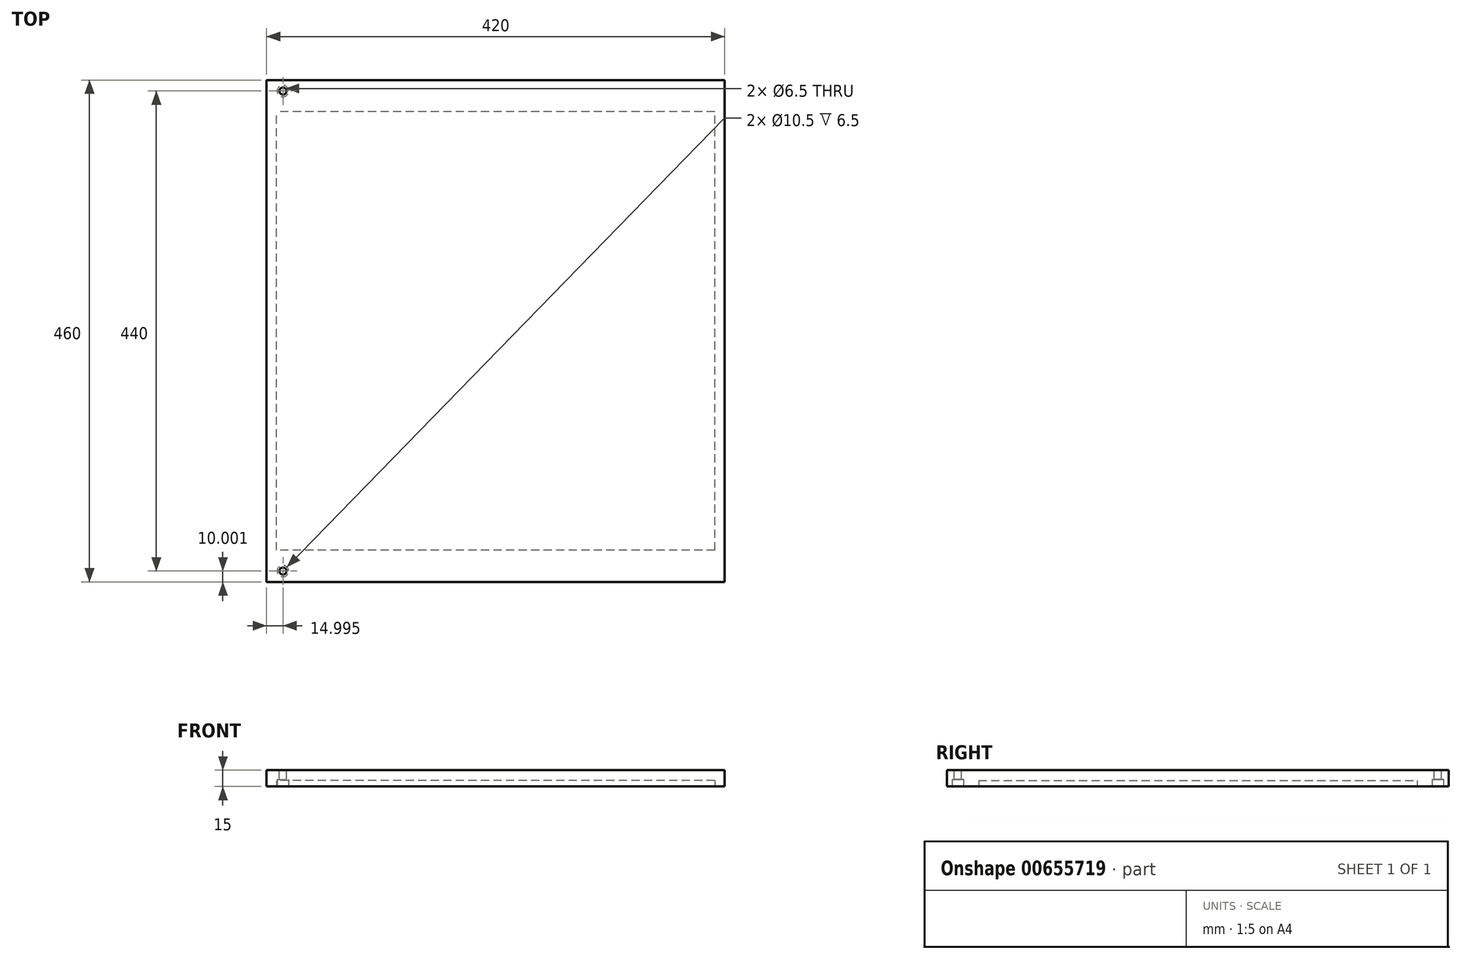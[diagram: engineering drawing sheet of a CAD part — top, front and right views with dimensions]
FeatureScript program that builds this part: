
annotation { "Feature Type Name" : "Feature", "Feature Type Description" : "" }
export const myFeature = defineFeature(function(context is Context, id is Id, definition is map)
    precondition{}
    {
        {
            var Q0;
            Q0=qCreatedBy(makeId("Top.planeOp"),FACE);
            var sketch = newSketch(context, id + "F0", { "sketchPlane" : qUnion([Q0])});
            skLineSegment(sketch, "E0.bottom", {"start": v(-74.43, -51.4) * mm, "end": v(345.57, -51.4) * mm});
            skLineSegment(sketch, "E0.top", {"start": v(-74.43, 408.6) * mm, "end": v(345.57, 408.6) * mm});
            skLineSegment(sketch, "E0.left", {"start": v(-74.43, -51.4) * mm, "end": v(-74.43, 408.6) * mm});
            skLineSegment(sketch, "E0.right", {"start": v(345.57, -51.4) * mm, "end": v(345.57, 408.6) * mm});
            skSolve(sketch);
        }
        {
            var Q0;
            Q0=makeQuery(id+"F0.imprint","IMPRINT",FACE,{"disambiguationData":[TD([[makeQuery(id+"F0.imprint","IMPRINT",EDGE,{"derivedFrom":sQuery(id+"F0.wireOp",EDGE,"E0.bottom")}),1.0]])]});
            extrude(context, id + "F1", {"entities" : qUnion([Q0]), "depth" : 15 * mm, "offsetDistance" : 25 * mm});
        }
        {
            var Q0;
            Q0=makeQuery(id+"F1.opExtrude","CAP_FACE",FACE,{"disambiguationData":[OSD([sQuery(id+"F0.wireOp",EDGE,"E0.bottom"),sQuery(id+"F0.wireOp",EDGE,"E0.top"),sQuery(id+"F0.wireOp",EDGE,"E0.left"),sQuery(id+"F0.wireOp",EDGE,"E0.right")])],"isStart":false});
            var sketch = newSketch(context, id + "F2", { "sketchPlane" : qUnion([Q0])});
            skCircle(sketch, "E1", {"center": v(-59.43, -41.4) * mm, "radius": 3.25 * mm});
            skLineSegment(sketch, "E2", {"start": v(-74.43, 178.6) * mm, "end": v(345.57, 178.6) * mm});
            skCircle(sketch, "E3.MirrorC", {"center": v(-59.43, 398.6) * mm, "radius": 3.25 * mm});
            skSolve(sketch);
        }
        {
            var Q0;
            Q0=qSketchRegion(id+"F2",true);
            extrude(context, id + "F3", {"entities" : qUnion([Q0]), "operationType" : NewBodyOperationType.REMOVE, "oppositeDirection" : true, "depth" : 15 * mm, "offsetDistance" : 25 * mm});
        }
        {
            var Q0;
            Q0=makeQuery(id+"F1.opExtrude","CAP_FACE",FACE,{"disambiguationData":[OSD([sQuery(id+"F0.wireOp",EDGE,"E0.bottom"),sQuery(id+"F0.wireOp",EDGE,"E0.top"),sQuery(id+"F0.wireOp",EDGE,"E0.left"),sQuery(id+"F0.wireOp",EDGE,"E0.right")])],"isStart":true});
            var sketch = newSketch(context, id + "F4", { "sketchPlane" : qUnion([Q0])});
            skLineSegment(sketch, "E4.bottom", {"start": v(336.57, 22.4) * mm, "end": v(-65.43, 22.4) * mm});
            skLineSegment(sketch, "E4.top", {"start": v(336.57, -379.6) * mm, "end": v(-65.43, -379.6) * mm});
            skLineSegment(sketch, "E4.left", {"start": v(336.57, 22.4) * mm, "end": v(336.57, -379.6) * mm});
            skLineSegment(sketch, "E4.right", {"start": v(-65.43, 22.4) * mm, "end": v(-65.43, -379.6) * mm});
            skSolve(sketch);
        }
        {
            var Q0;
            Q0=makeQuery(id+"F4.imprint","IMPRINT",FACE,{"disambiguationData":[TD([[makeQuery(id+"F4.imprint","IMPRINT",EDGE,{"derivedFrom":sQuery(id+"F4.wireOp",EDGE,"E4.bottom")}),1.0]])]});
            extrude(context, id + "F5", {"entities" : qUnion([Q0]), "operationType" : NewBodyOperationType.REMOVE, "oppositeDirection" : true, "depth" : 5.5 * mm, "offsetDistance" : 25 * mm});
        }
        {
            var Q0;
            Q0=makeQuery(id+"F1.opExtrude","CAP_FACE",FACE,{"disambiguationData":[OSD([sQuery(id+"F0.wireOp",EDGE,"E0.bottom"),sQuery(id+"F0.wireOp",EDGE,"E0.top"),sQuery(id+"F0.wireOp",EDGE,"E0.left"),sQuery(id+"F0.wireOp",EDGE,"E0.right")])],"isStart":true});
            var sketch = newSketch(context, id + "F6", { "sketchPlane" : qUnion([Q0])});
            skCircle(sketch, "E5", {"center": v(-59.43, -398.6) * mm, "radius": 5.25 * mm});
            skCircle(sketch, "E6", {"center": v(-59.43, 41.4) * mm, "radius": 5.25 * mm});
            skSolve(sketch);
        }
        {
            var Q0;
            Q0 = qSketchRegion(id + "F6", true);
            extrude(context, id + "F7", {"entities" : qUnion([Q0]), "operationType" : NewBodyOperationType.REMOVE, "oppositeDirection" : true, "depth" : 6.5 * mm, "offsetDistance" : 25 * mm});
        }
        {
            var Q0;
            Q0 = qSketchRegion(id + "F6", true);
            extrude(context, id + "F8", {"entities" : qUnion([Q0]), "operationType" : NewBodyOperationType.REMOVE, "oppositeDirection" : true, "depth" : 6.5 * mm, "offsetDistance" : 25 * mm});
        }
    });
